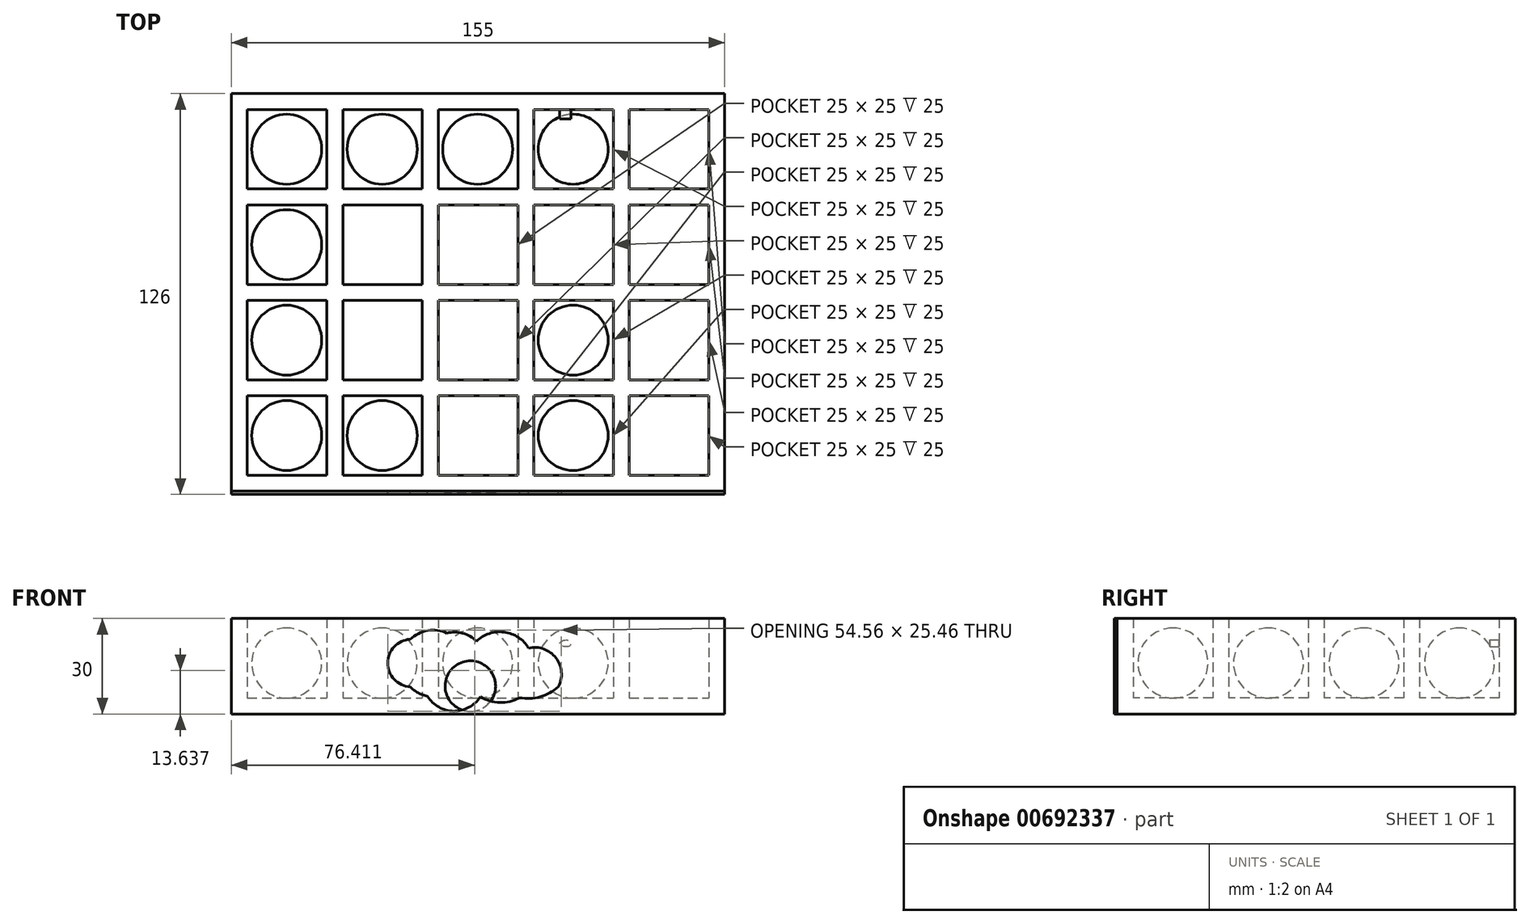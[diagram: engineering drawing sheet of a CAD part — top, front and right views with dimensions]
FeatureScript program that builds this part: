
annotation { "Feature Type Name" : "Feature", "Feature Type Description" : "" }
export const myFeature = defineFeature(function(context is Context, id is Id, definition is map)
    precondition{}
    {
        {
            assignVariable(context, id + "F0", {"name" : "cube", "anyValue" : 25});
        }
        {
            assignVariable(context, id + "F1", {"name" : "wall", "anyValue" : 5});
        }
        {
            var Q0;
            Q0=qCreatedBy(makeId("Top.planeOp"),FACE);
            var sketch = newSketch(context, id + "F2", { "sketchPlane" : qUnion([Q0])});
            skLineSegment(sketch, "E0.bottom", {"start": v(-76.57, 49.75) * mm, "end": v(78.43, 49.75) * mm});
            skLineSegment(sketch, "E0.top", {"start": v(-76.57, -75.25) * mm, "end": v(78.43, -75.25) * mm});
            skLineSegment(sketch, "E0.left", {"start": v(-76.57, 49.75) * mm, "end": v(-76.57, -75.25) * mm});
            skLineSegment(sketch, "E0.right", {"start": v(78.43, 49.75) * mm, "end": v(78.43, -75.25) * mm});
            skSolve(sketch);
        }
        {
            var Q0;
            Q0=makeQuery(id+"F2.imprint","IMPRINT",FACE,{"disambiguationData":[TD([[makeQuery(id+"F2.imprint","IMPRINT",EDGE,{"derivedFrom":sQuery(id+"F2.wireOp",EDGE,"E0.bottom")}),-1.0]])]});
            extrude(context, id + "F3", {"entities" : qUnion([Q0]), "depth" : (getVariable(context, 'wall')) * mm, "offsetDistance" : 25 * mm});
        }
        {
            var Q0;
            Q0=makeQuery(id+"F3.opExtrude","CAP_FACE",FACE,{"disambiguationData":[OSD([sQuery(id+"F2.wireOp",EDGE,"E0.bottom"),sQuery(id+"F2.wireOp",EDGE,"E0.top"),sQuery(id+"F2.wireOp",EDGE,"E0.left"),sQuery(id+"F2.wireOp",EDGE,"E0.right")])],"isStart":false});
            var sketch = newSketch(context, id + "F4", { "sketchPlane" : qUnion([Q0])});
            skLineSegment(sketch, "E1.bottom", {"start": v(-71.57, 44.75) * mm, "end": v(-46.57, 44.75) * mm});
            skLineSegment(sketch, "E1.top", {"start": v(-71.57, 19.75) * mm, "end": v(-46.57, 19.75) * mm});
            skLineSegment(sketch, "E1.left", {"start": v(-71.57, 44.75) * mm, "end": v(-71.57, 19.75) * mm});
            skLineSegment(sketch, "E1.right", {"start": v(-46.57, 44.75) * mm, "end": v(-46.57, 19.75) * mm});
            skLineSegment(sketch, "E2.0.1.0", {"start": v(-46.57, 14.75) * mm, "end": v(-46.57, -10.25) * mm});
            skLineSegment(sketch, "E2.0.1.1", {"start": v(-71.57, 14.75) * mm, "end": v(-71.57, -10.25) * mm});
            skLineSegment(sketch, "E2.0.1.2", {"start": v(-71.57, -10.25) * mm, "end": v(-46.57, -10.25) * mm});
            skLineSegment(sketch, "E2.0.1.3", {"start": v(-71.57, 14.75) * mm, "end": v(-46.57, 14.75) * mm});
            skLineSegment(sketch, "E2.0.2.0", {"start": v(-46.57, -15.25) * mm, "end": v(-46.57, -40.25) * mm});
            skLineSegment(sketch, "E2.0.2.1", {"start": v(-71.57, -15.25) * mm, "end": v(-71.57, -40.25) * mm});
            skLineSegment(sketch, "E2.0.2.2", {"start": v(-71.57, -40.25) * mm, "end": v(-46.57, -40.25) * mm});
            skLineSegment(sketch, "E2.0.2.3", {"start": v(-71.57, -15.25) * mm, "end": v(-46.57, -15.25) * mm});
            skLineSegment(sketch, "E2.0.3.0", {"start": v(-46.57, -45.25) * mm, "end": v(-46.57, -70.25) * mm});
            skLineSegment(sketch, "E2.0.3.1", {"start": v(-71.57, -45.25) * mm, "end": v(-71.57, -70.25) * mm});
            skLineSegment(sketch, "E2.0.3.2", {"start": v(-71.57, -70.25) * mm, "end": v(-46.57, -70.25) * mm});
            skLineSegment(sketch, "E2.0.3.3", {"start": v(-71.57, -45.25) * mm, "end": v(-46.57, -45.25) * mm});
            skLineSegment(sketch, "E2.1.0.0", {"start": v(-16.57, 44.75) * mm, "end": v(-16.57, 19.75) * mm});
            skLineSegment(sketch, "E2.1.0.1", {"start": v(-41.57, 44.75) * mm, "end": v(-41.57, 19.75) * mm});
            skLineSegment(sketch, "E2.1.0.2", {"start": v(-41.57, 19.75) * mm, "end": v(-16.57, 19.75) * mm});
            skLineSegment(sketch, "E2.1.0.3", {"start": v(-41.57, 44.75) * mm, "end": v(-16.57, 44.75) * mm});
            skLineSegment(sketch, "E2.1.1.0", {"start": v(-16.57, 14.75) * mm, "end": v(-16.57, -10.25) * mm});
            skLineSegment(sketch, "E2.1.1.1", {"start": v(-41.57, 14.75) * mm, "end": v(-41.57, -10.25) * mm});
            skLineSegment(sketch, "E2.1.1.2", {"start": v(-41.57, -10.25) * mm, "end": v(-16.57, -10.25) * mm});
            skLineSegment(sketch, "E2.1.1.3", {"start": v(-41.57, 14.75) * mm, "end": v(-16.57, 14.75) * mm});
            skLineSegment(sketch, "E2.1.2.0", {"start": v(-16.57, -15.25) * mm, "end": v(-16.57, -40.25) * mm});
            skLineSegment(sketch, "E2.1.2.1", {"start": v(-41.57, -15.25) * mm, "end": v(-41.57, -40.25) * mm});
            skLineSegment(sketch, "E2.1.2.2", {"start": v(-41.57, -40.25) * mm, "end": v(-16.57, -40.25) * mm});
            skLineSegment(sketch, "E2.1.2.3", {"start": v(-41.57, -15.25) * mm, "end": v(-16.57, -15.25) * mm});
            skLineSegment(sketch, "E2.1.3.0", {"start": v(-16.57, -45.25) * mm, "end": v(-16.57, -70.25) * mm});
            skLineSegment(sketch, "E2.1.3.1", {"start": v(-41.57, -45.25) * mm, "end": v(-41.57, -70.25) * mm});
            skLineSegment(sketch, "E2.1.3.2", {"start": v(-41.57, -70.25) * mm, "end": v(-16.57, -70.25) * mm});
            skLineSegment(sketch, "E2.1.3.3", {"start": v(-41.57, -45.25) * mm, "end": v(-16.57, -45.25) * mm});
            skLineSegment(sketch, "E2.2.0.0", {"start": v(13.43, 44.75) * mm, "end": v(13.43, 19.75) * mm});
            skLineSegment(sketch, "E2.2.0.1", {"start": v(-11.57, 44.75) * mm, "end": v(-11.57, 19.75) * mm});
            skLineSegment(sketch, "E2.2.0.2", {"start": v(-11.57, 19.75) * mm, "end": v(13.43, 19.75) * mm});
            skLineSegment(sketch, "E2.2.0.3", {"start": v(-11.57, 44.75) * mm, "end": v(13.43, 44.75) * mm});
            skLineSegment(sketch, "E2.2.1.0", {"start": v(13.43, 14.75) * mm, "end": v(13.43, -10.25) * mm});
            skLineSegment(sketch, "E2.2.1.1", {"start": v(-11.57, 14.75) * mm, "end": v(-11.57, -10.25) * mm});
            skLineSegment(sketch, "E2.2.1.2", {"start": v(-11.57, -10.25) * mm, "end": v(13.43, -10.25) * mm});
            skLineSegment(sketch, "E2.2.1.3", {"start": v(-11.57, 14.75) * mm, "end": v(13.43, 14.75) * mm});
            skLineSegment(sketch, "E2.2.2.0", {"start": v(13.43, -15.25) * mm, "end": v(13.43, -40.25) * mm});
            skLineSegment(sketch, "E2.2.2.1", {"start": v(-11.57, -15.25) * mm, "end": v(-11.57, -40.25) * mm});
            skLineSegment(sketch, "E2.2.2.2", {"start": v(-11.57, -40.25) * mm, "end": v(13.43, -40.25) * mm});
            skLineSegment(sketch, "E2.2.2.3", {"start": v(-11.57, -15.25) * mm, "end": v(13.43, -15.25) * mm});
            skLineSegment(sketch, "E2.2.3.0", {"start": v(13.43, -45.25) * mm, "end": v(13.43, -70.25) * mm});
            skLineSegment(sketch, "E2.2.3.1", {"start": v(-11.57, -45.25) * mm, "end": v(-11.57, -70.25) * mm});
            skLineSegment(sketch, "E2.2.3.2", {"start": v(-11.57, -70.25) * mm, "end": v(13.43, -70.25) * mm});
            skLineSegment(sketch, "E2.2.3.3", {"start": v(-11.57, -45.25) * mm, "end": v(13.43, -45.25) * mm});
            skLineSegment(sketch, "E2.3.0.0", {"start": v(43.43, 44.75) * mm, "end": v(43.43, 19.75) * mm});
            skLineSegment(sketch, "E2.3.0.1", {"start": v(18.43, 44.75) * mm, "end": v(18.43, 19.75) * mm});
            skLineSegment(sketch, "E2.3.0.2", {"start": v(18.43, 19.75) * mm, "end": v(43.43, 19.75) * mm});
            skLineSegment(sketch, "E2.3.0.3", {"start": v(18.43, 44.75) * mm, "end": v(43.43, 44.75) * mm});
            skLineSegment(sketch, "E2.3.1.0", {"start": v(43.43, 14.75) * mm, "end": v(43.43, -10.25) * mm});
            skLineSegment(sketch, "E2.3.1.1", {"start": v(18.43, 14.75) * mm, "end": v(18.43, -10.25) * mm});
            skLineSegment(sketch, "E2.3.1.2", {"start": v(18.43, -10.25) * mm, "end": v(43.43, -10.25) * mm});
            skLineSegment(sketch, "E2.3.1.3", {"start": v(18.43, 14.75) * mm, "end": v(43.43, 14.75) * mm});
            skLineSegment(sketch, "E2.3.2.0", {"start": v(43.43, -15.25) * mm, "end": v(43.43, -40.25) * mm});
            skLineSegment(sketch, "E2.3.2.1", {"start": v(18.43, -15.25) * mm, "end": v(18.43, -40.25) * mm});
            skLineSegment(sketch, "E2.3.2.2", {"start": v(18.43, -40.25) * mm, "end": v(43.43, -40.25) * mm});
            skLineSegment(sketch, "E2.3.2.3", {"start": v(18.43, -15.25) * mm, "end": v(43.43, -15.25) * mm});
            skLineSegment(sketch, "E2.3.3.0", {"start": v(43.43, -45.25) * mm, "end": v(43.43, -70.25) * mm});
            skLineSegment(sketch, "E2.3.3.1", {"start": v(18.43, -45.25) * mm, "end": v(18.43, -70.25) * mm});
            skLineSegment(sketch, "E2.3.3.2", {"start": v(18.43, -70.25) * mm, "end": v(43.43, -70.25) * mm});
            skLineSegment(sketch, "E2.3.3.3", {"start": v(18.43, -45.25) * mm, "end": v(43.43, -45.25) * mm});
            skLineSegment(sketch, "E2.4.0.0", {"start": v(73.43, 44.75) * mm, "end": v(73.43, 19.75) * mm});
            skLineSegment(sketch, "E2.4.0.1", {"start": v(48.43, 44.75) * mm, "end": v(48.43, 19.75) * mm});
            skLineSegment(sketch, "E2.4.0.2", {"start": v(48.43, 19.75) * mm, "end": v(73.43, 19.75) * mm});
            skLineSegment(sketch, "E2.4.0.3", {"start": v(48.43, 44.75) * mm, "end": v(73.43, 44.75) * mm});
            skLineSegment(sketch, "E2.4.1.0", {"start": v(73.43, 14.75) * mm, "end": v(73.43, -10.25) * mm});
            skLineSegment(sketch, "E2.4.1.1", {"start": v(48.43, 14.75) * mm, "end": v(48.43, -10.25) * mm});
            skLineSegment(sketch, "E2.4.1.2", {"start": v(48.43, -10.25) * mm, "end": v(73.43, -10.25) * mm});
            skLineSegment(sketch, "E2.4.1.3", {"start": v(48.43, 14.75) * mm, "end": v(73.43, 14.75) * mm});
            skLineSegment(sketch, "E2.4.2.0", {"start": v(73.43, -15.25) * mm, "end": v(73.43, -40.25) * mm});
            skLineSegment(sketch, "E2.4.2.1", {"start": v(48.43, -15.25) * mm, "end": v(48.43, -40.25) * mm});
            skLineSegment(sketch, "E2.4.2.2", {"start": v(48.43, -40.25) * mm, "end": v(73.43, -40.25) * mm});
            skLineSegment(sketch, "E2.4.2.3", {"start": v(48.43, -15.25) * mm, "end": v(73.43, -15.25) * mm});
            skLineSegment(sketch, "E2.4.3.0", {"start": v(73.43, -45.25) * mm, "end": v(73.43, -70.25) * mm});
            skLineSegment(sketch, "E2.4.3.1", {"start": v(48.43, -45.25) * mm, "end": v(48.43, -70.25) * mm});
            skLineSegment(sketch, "E2.4.3.2", {"start": v(48.43, -70.25) * mm, "end": v(73.43, -70.25) * mm});
            skLineSegment(sketch, "E2.4.3.3", {"start": v(48.43, -45.25) * mm, "end": v(73.43, -45.25) * mm});
            skLineSegment(sketch, "E2.direction1", {"start": v(-71.57, 19.75) * mm, "end": v(-41.57, 19.75) * mm, "construction": true});
            skLineSegment(sketch, "E2.direction2", {"start": v(-71.57, 19.75) * mm, "end": v(-71.57, -10.25) * mm, "construction": true});
            skSolve(sketch);
        }
        {
            var Q0;
            Q0=makeQuery(id+"F4.imprint","IMPRINT",FACE,{"disambiguationData":[TD([[makeQuery(id+"F4.imprint","IMPRINT",EDGE,{"derivedFrom":sQuery(id+"F4.wireOp",EDGE,"E1.bottom")}),1.0]])]});
            extrude(context, id + "F5", {"entities" : qUnion([Q0]), "operationType" : NewBodyOperationType.ADD, "depth" : (getVariable(context, 'cube')) * mm, "offsetDistance" : 25 * mm});
        }
        {
            var Q0;
            Q0=makeQuery(id+"F5.opExtrude","SWEPT_FACE",FACE,{"disambiguationData":[OSD([sQuery(id+"F4.wireOp",EDGE,"E1.bottom")])]});
            cPlane(context, id + "F6", {"entities" : qUnion([Q0]), "cplaneType" : CPlaneType.OFFSET, "offset" : (getVariable(context, 'cube') / 2) * mm, "width" : 150 * mm, "height" : 150 * mm});
        }
        {
            var Q0;
            Q0=qCreatedBy(id+"F6.planeOp",FACE);
            var sketch = newSketch(context, id + "F7", { "sketchPlane" : qUnion([Q0])});
            skArc(sketch, "E3", {"start": v(-59.2, 5) * mm, "mid": v(-48.2, 16) * mm, "end": v(-59.2, 27) * mm});
            skLineSegment(sketch, "E4", {"start": v(-59.2, 5) * mm, "end": v(-59.2, 27) * mm});
            skSolve(sketch);
        }
        {
            var Q0;
            Q0=makeQuery(id+"F7.imprint","IMPRINT",FACE,{"disambiguationData":[TD([[makeQuery(id+"F7.imprint","IMPRINT",EDGE,{"derivedFrom":sQuery(id+"F7.wireOp",EDGE,"E3")}),1.0]])]});
            var Q1;
            Q1=sQuery(id+"F7.wireOp",EDGE,"E4");
            revolve(context, id + "F8", {"entities" : qUnion([Q0]), "axis" : qUnion([Q1]), "revolveType" : RevolveType.FULL});
        }
        {
            var Q0;
            Q0=makeQuery(id+"F8.opRevolve","SWEPT_BODY",BODY,{"disambiguationData":[OSD([sQuery(id+"F7.wireOp",EDGE,"E3"),sQuery(id+"F7.wireOp",EDGE,"E4")])]});
            transform(context, id + "F9", {"entities" : qUnion([Q0]), "transformType" : TransformType.TRANSLATION_3D, "dx" : 30 * mm, "dy" : 0 * mm, "dz" : 0 * mm, "makeCopy" : true});
        }
        {
            var Q0;
            Q0=makeQuery(id+"F9.opPattern","COPY",BODY,{"derivedFrom":makeQuery(id+"F8.opRevolve","SWEPT_BODY",BODY,{"disambiguationData":[OSD([sQuery(id+"F7.wireOp",EDGE,"E3"),sQuery(id+"F7.wireOp",EDGE,"E4")])]}),"instanceName":"1"});
            transform(context, id + "F10", {"entities" : qUnion([Q0]), "transformType" : TransformType.TRANSLATION_3D, "dx" : 30 * mm, "dy" : 0 * mm, "dz" : 0 * mm, "makeCopy" : true});
        }
        {
            var Q0;
            Q0=makeQuery(id+"F10.opPattern","COPY",BODY,{"derivedFrom":makeQuery(id+"F9.opPattern","COPY",BODY,{"derivedFrom":makeQuery(id+"F8.opRevolve","SWEPT_BODY",BODY,{"disambiguationData":[OSD([sQuery(id+"F7.wireOp",EDGE,"E3"),sQuery(id+"F7.wireOp",EDGE,"E4")])]}),"instanceName":"1"}),"instanceName":"1"});
            transform(context, id + "F11", {"entities" : qUnion([Q0]), "transformType" : TransformType.TRANSLATION_3D, "dx" : 30 * mm, "dy" : 0 * mm, "dz" : 0 * mm, "makeCopy" : true});
        }
        {
            var Q0;
            Q0=makeQuery(id+"F5.opExtrude","SWEPT_FACE",FACE,{"disambiguationData":[OSD([sQuery(id+"F4.wireOp",EDGE,"E2.3.0.3")])]});
            var sketch = newSketch(context, id + "F12", { "sketchPlane" : qUnion([Q0])});
            skFitSpline(sketch, "E5", {"points": [v(26.6, 22.2) * mm, v(28.87, 23.25) * mm, v(30.06, 21.8) * mm, v(28.18, 21.17) * mm, v(26.6, 22.2) * mm]});
            skSolve(sketch);
        }
        {
            var Q0;
            Q0=makeQuery(id+"F12.imprint","IMPRINT",FACE,{"disambiguationData":[TD([[makeQuery(id+"F12.imprint","IMPRINT",EDGE,{"derivedFrom":sQuery(id+"F12.wireOp",EDGE,"E5")}),-1.0]])]});
            extrude(context, id + "F13", {"entities" : qUnion([Q0]), "depth" : 3 * mm, "offsetDistance" : 25 * mm});
        }
        {
            var Q0;
            Q0=makeQuery(id+"F8.opRevolve","SWEPT_BODY",BODY,{"disambiguationData":[OSD([sQuery(id+"F7.wireOp",EDGE,"E3"),sQuery(id+"F7.wireOp",EDGE,"E4")])]});
            transform(context, id + "F14", {"entities" : qUnion([Q0]), "transformType" : TransformType.TRANSLATION_3D, "dx" : 0 * mm, "dy" : -30 * mm, "dz" : 0 * mm, "makeCopy" : true});
        }
        {
            var Q0;
            Q0=makeQuery(id+"F14.opPattern","COPY",BODY,{"derivedFrom":makeQuery(id+"F8.opRevolve","SWEPT_BODY",BODY,{"disambiguationData":[OSD([sQuery(id+"F7.wireOp",EDGE,"E3"),sQuery(id+"F7.wireOp",EDGE,"E4")])]}),"instanceName":"1"});
            transform(context, id + "F15", {"entities" : qUnion([Q0]), "transformType" : TransformType.TRANSLATION_3D, "dx" : 0 * mm, "dy" : -30 * mm, "dz" : 0 * mm, "makeCopy" : true});
        }
        {
            var Q0;
            Q0=makeQuery(id+"F15.opPattern","COPY",BODY,{"derivedFrom":makeQuery(id+"F14.opPattern","COPY",BODY,{"derivedFrom":makeQuery(id+"F8.opRevolve","SWEPT_BODY",BODY,{"disambiguationData":[OSD([sQuery(id+"F7.wireOp",EDGE,"E3"),sQuery(id+"F7.wireOp",EDGE,"E4")])]}),"instanceName":"1"}),"instanceName":"1"});
            transform(context, id + "F16", {"entities" : qUnion([Q0]), "transformType" : TransformType.TRANSLATION_3D, "dx" : 90 * mm, "dy" : 0 * mm, "dz" : 0 * mm, "makeCopy" : true});
        }
        {
            var Q0;
            Q0=makeQuery(id+"F15.opPattern","COPY",BODY,{"derivedFrom":makeQuery(id+"F14.opPattern","COPY",BODY,{"derivedFrom":makeQuery(id+"F8.opRevolve","SWEPT_BODY",BODY,{"disambiguationData":[OSD([sQuery(id+"F7.wireOp",EDGE,"E3"),sQuery(id+"F7.wireOp",EDGE,"E4")])]}),"instanceName":"1"}),"instanceName":"1"});
            transform(context, id + "F17", {"entities" : qUnion([Q0]), "transformType" : TransformType.TRANSLATION_3D, "dx" : 0 * mm, "dy" : -30 * mm, "dz" : 0 * mm, "makeCopy" : true});
        }
        {
            var Q0;
            Q0=makeQuery(id+"F17.opPattern","COPY",BODY,{"derivedFrom":makeQuery(id+"F15.opPattern","COPY",BODY,{"derivedFrom":makeQuery(id+"F14.opPattern","COPY",BODY,{"derivedFrom":makeQuery(id+"F8.opRevolve","SWEPT_BODY",BODY,{"disambiguationData":[OSD([sQuery(id+"F7.wireOp",EDGE,"E3"),sQuery(id+"F7.wireOp",EDGE,"E4")])]}),"instanceName":"1"}),"instanceName":"1"}),"instanceName":"1"});
            transform(context, id + "F18", {"entities" : qUnion([Q0]), "transformType" : TransformType.TRANSLATION_3D, "dx" : 30 * mm, "dy" : 0 * mm, "dz" : 0 * mm, "makeCopy" : true});
        }
        {
            var Q0;
            Q0=makeQuery(id+"F18.opPattern","COPY",BODY,{"derivedFrom":makeQuery(id+"F17.opPattern","COPY",BODY,{"derivedFrom":makeQuery(id+"F15.opPattern","COPY",BODY,{"derivedFrom":makeQuery(id+"F14.opPattern","COPY",BODY,{"derivedFrom":makeQuery(id+"F8.opRevolve","SWEPT_BODY",BODY,{"disambiguationData":[OSD([sQuery(id+"F7.wireOp",EDGE,"E3"),sQuery(id+"F7.wireOp",EDGE,"E4")])]}),"instanceName":"1"}),"instanceName":"1"}),"instanceName":"1"}),"instanceName":"1"});
            transform(context, id + "F19", {"entities" : qUnion([Q0]), "transformType" : TransformType.TRANSLATION_3D, "dx" : 60 * mm, "dy" : 0 * mm, "dz" : 0 * mm, "makeCopy" : true});
        }
        {
            var Q0;
            {var subQ0=sQuery(id+"F2.wireOp",EDGE,"E0.top");Q0=makeQuery(id+"F5.boolean.opBoolean","MERGE",FACE,{"derivedFrom":[makeQuery(id+"F3.opExtrude","SWEPT_FACE",FACE,{"disambiguationData":[OSD([subQ0])]}),makeQuery(id+"F5.opExtrude","SWEPT_FACE",FACE,{"disambiguationData":[OSD([subQ0])]})]});}
            var sketch = newSketch(context, id + "F20", { "sketchPlane" : qUnion([Q0])});
            skArc(sketch, "E6", {"start": v(-20.38, 23.46) * mm, "mid": v(-14.9, 26.23) * mm, "end": v(-8.82, 25.4) * mm});
            skArc(sketch, "E7", {"start": v(-20.38, 23.46) * mm, "mid": v(-27.44, 16) * mm, "end": v(-20.38, 8.55) * mm});
            skArc(sketch, "E8", {"start": v(-20.38, 8.55) * mm, "mid": v(-14.95, 5.6) * mm, "end": v(-8.82, 6.45) * mm});
            skArc(sketch, "E9", {"start": v(-8.82, 6.45) * mm, "mid": v(-3.86, 4.5) * mm, "end": v(1.36, 5.6) * mm});
            skArc(sketch, "E10", {"start": v(1.36, 5.6) * mm, "mid": v(7.6, 3.61) * mm, "end": v(13.99, 5.1) * mm});
            skArc(sketch, "E11", {"start": v(16.83, 20.71) * mm, "mid": v(25.4, 17.63) * mm, "end": v(26.19, 8.55) * mm});
            skArc(sketch, "E12", {"start": v(26.19, 8.55) * mm, "mid": v(20.49, 5.42) * mm, "end": v(13.99, 5.1) * mm});
            skArc(sketch, "E13", {"start": v(-8.82, 25.4) * mm, "mid": v(-3.87, 25.37) * mm, "end": v(0.4, 22.86) * mm});
            skArc(sketch, "E14", {"start": v(16.83, 20.71) * mm, "mid": v(9.13, 25.72) * mm, "end": v(0.4, 22.86) * mm});
            skArc(sketch, "E15", {"start": v(-14.95, 5.6) * mm, "mid": v(-6.7, 0.9) * mm, "end": v(1.63, 5.42) * mm});
            skSolve(sketch);
        }
        {
            var Q0;
            Q0=makeQuery(id+"F20.imprint","IMPRINT",FACE,{"disambiguationData":[TD([[makeQuery(id+"F20.imprint","IMPRINT",EDGE,{"derivedFrom":sQuery(id+"F20.wireOp",EDGE,"E6")}),-1.0]])]});
            extrude(context, id + "F21", {"entities" : qUnion([Q0]), "depth" : 1 * mm, "offsetDistance" : 25 * mm});
        }
        {
            var Q0;
            {var subQ0=sQuery(id+"F2.wireOp",EDGE,"E0.top");Q0=makeQuery(id+"F5.boolean.opBoolean","MERGE",FACE,{"derivedFrom":[makeQuery(id+"F3.opExtrude","SWEPT_FACE",FACE,{"disambiguationData":[OSD([subQ0])]}),makeQuery(id+"F5.opExtrude","SWEPT_FACE",FACE,{"disambiguationData":[OSD([subQ0])]})]});}
            var sketch = newSketch(context, id + "F22", { "sketchPlane" : qUnion([Q0])});
            skCircle(sketch, "E16", {"center": v(-1.49, 8.77) * mm, "radius": 7.93 * mm});
            skSolve(sketch);
        }
        {
            var Q0;
            Q0=makeQuery(id+"F22.imprint","IMPRINT",FACE,{"disambiguationData":[TD([[makeQuery(id+"F22.imprint","IMPRINT",EDGE,{"derivedFrom":sQuery(id+"F22.wireOp",EDGE,"E16")}),1.0]])]});
            extrude(context, id + "F23", {"entities" : qUnion([Q0]), "depth" : 0.75 * mm, "offsetDistance" : 25 * mm});
        }
    });
